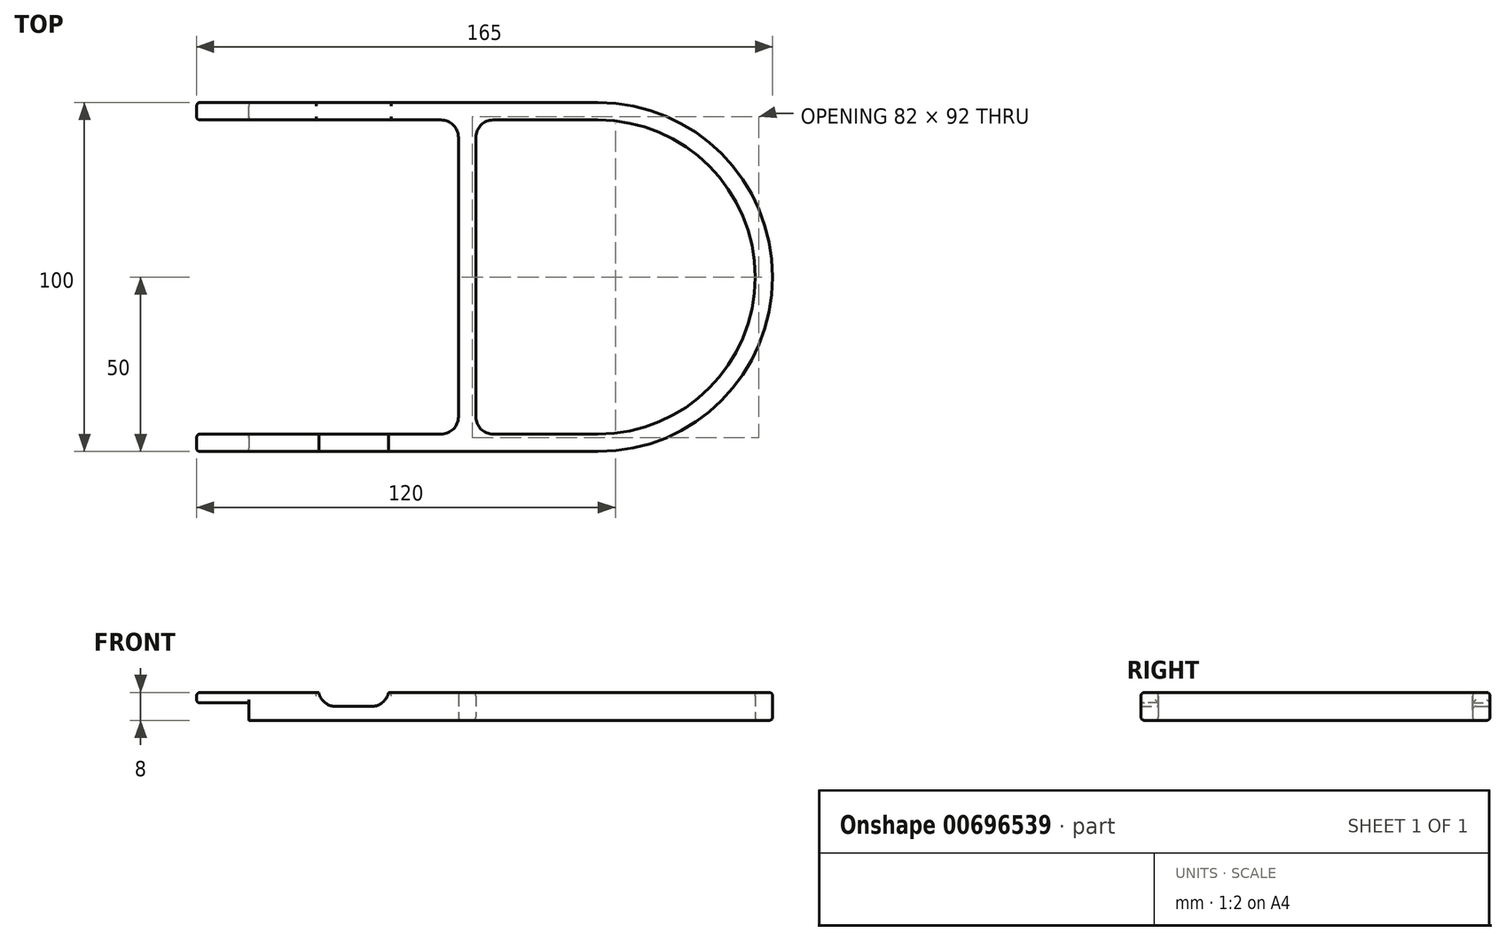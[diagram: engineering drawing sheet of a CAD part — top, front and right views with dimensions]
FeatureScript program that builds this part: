
annotation { "Feature Type Name" : "Feature", "Feature Type Description" : "" }
export const myFeature = defineFeature(function(context is Context, id is Id, definition is map)
    precondition{}
    {
        {
            var Q0;
            Q0=qCreatedBy(makeId("Top.planeOp"),FACE);
            var sketch = newSketch(context, id + "F0", { "sketchPlane" : qUnion([Q0])});
            skLineSegment(sketch, "E0", {"start": v(0, 0) * mm, "end": v(100, 0) * mm});
            skArc(sketch, "E1", {"start": v(100, 0) * mm, "mid": v(145, 45) * mm, "end": v(100, 90) * mm});
            skLineSegment(sketch, "E2", {"start": v(100, 90) * mm, "end": v(0, 90) * mm});
            skLineSegment(sketch, "E3", {"start": v(0, 90) * mm, "end": v(0, 95) * mm});
            skLineSegment(sketch, "E4", {"start": v(0, 95) * mm, "end": v(100, 95) * mm});
            skArc(sketch, "E5", {"start": v(100, -5) * mm, "mid": v(150, 45) * mm, "end": v(100, 95) * mm});
            skLineSegment(sketch, "E6", {"start": v(0, 0) * mm, "end": v(0, -5) * mm});
            skLineSegment(sketch, "E7", {"start": v(0, -5) * mm, "end": v(100, -5) * mm});
            skLineSegment(sketch, "E8.bottom", {"start": v(60, 0) * mm, "end": v(65, 0) * mm});
            skLineSegment(sketch, "E8.top", {"start": v(60, 90) * mm, "end": v(65, 90) * mm});
            skLineSegment(sketch, "E8.left", {"start": v(60, 0) * mm, "end": v(60, 90) * mm});
            skLineSegment(sketch, "E8.right", {"start": v(65, 0) * mm, "end": v(65, 90) * mm});
            skSolve(sketch);
        }
        {
            var Q0;
            Q0 = qSketchRegion(id + "F0", true);
            extrude(context, id + "F1", {"entities" : qUnion([Q0]), "depth" : 8 * mm, "offsetDistance" : 25 * mm});
        }
        {
            var Q0;
            Q0=makeQuery(id+"F1.opExtrude","SWEPT_FACE",FACE,{"disambiguationData":[OSD([sQuery(id+"F0.wireOp",EDGE,"E6")])]});
            var sketch = newSketch(context, id + "F2", { "sketchPlane" : qUnion([Q0])});
            skLineSegment(sketch, "E9.bottom", {"start": v(0, 8) * mm, "end": v(5, 8) * mm});
            skLineSegment(sketch, "E9.top", {"start": v(0, 5) * mm, "end": v(5, 5) * mm});
            skLineSegment(sketch, "E9.left", {"start": v(0, 8) * mm, "end": v(0, 5) * mm});
            skLineSegment(sketch, "E9.right", {"start": v(5, 8) * mm, "end": v(5, 5) * mm});
            skLineSegment(sketch, "E10.bottom", {"start": v(-90, 5) * mm, "end": v(-95, 5) * mm});
            skLineSegment(sketch, "E10.top", {"start": v(-90, 8) * mm, "end": v(-95, 8) * mm});
            skLineSegment(sketch, "E10.left", {"start": v(-90, 5) * mm, "end": v(-90, 8) * mm});
            skLineSegment(sketch, "E10.right", {"start": v(-95, 5) * mm, "end": v(-95, 8) * mm});
            skSolve(sketch);
        }
        {
            var Q0;
            Q0 = qSketchRegion(id + "F2", true);
            extrude(context, id + "F3", {"entities" : qUnion([Q0]), "operationType" : NewBodyOperationType.ADD, "depth" : 15 * mm, "offsetDistance" : 25 * mm});
        }
        {
            var Q0;
            Q0=makeQuery(id+"F1.opExtrude","SWEPT_EDGE",EDGE,{"disambiguationData":[OSD([sQuery(id+"F0.wireOp",EDGE,"E2"),sQuery(id+"F0.wireOp",EDGE,"E8.top"),sQuery(id+"F0.wireOp",EDGE,"E8.left")])]});
            var Q1;
            Q1=makeQuery(id+"F1.opExtrude","SWEPT_EDGE",EDGE,{"disambiguationData":[OSD([sQuery(id+"F0.wireOp",EDGE,"E2"),sQuery(id+"F0.wireOp",EDGE,"E8.top"),sQuery(id+"F0.wireOp",EDGE,"E8.right")])]});
            var Q2;
            Q2=makeQuery(id+"F1.opExtrude","SWEPT_EDGE",EDGE,{"disambiguationData":[OSD([sQuery(id+"F0.wireOp",EDGE,"E0"),sQuery(id+"F0.wireOp",EDGE,"E8.bottom"),sQuery(id+"F0.wireOp",EDGE,"E8.right")])]});
            var Q3;
            Q3=makeQuery(id+"F1.opExtrude","SWEPT_EDGE",EDGE,{"disambiguationData":[OSD([sQuery(id+"F0.wireOp",EDGE,"E0"),sQuery(id+"F0.wireOp",EDGE,"E8.bottom"),sQuery(id+"F0.wireOp",EDGE,"E8.left")])]});
            fillet(context, id + "F4", {"entities" : qUnion([Q0, Q1, Q2, Q3]), "radius" : 5 * mm, "tangentPropagation" : true, "allowEdgeOverflow" : false});
        }
        {
            var Q0;
            Q0=makeQuery(id+"F3.boolean.opBoolean","MERGE",FACE,{"derivedFrom":[makeQuery(id+"F1.opExtrude","SWEPT_FACE",FACE,{"disambiguationData":[OSD([sQuery(id+"F0.wireOp",EDGE,"E7")])]}),makeQuery(id+"F3.opExtrude","SWEPT_FACE",FACE,{"disambiguationData":[OSD([sQuery(id+"F2.wireOp",EDGE,"E9.right")])]})]});
            var sketch = newSketch(context, id + "F5", { "sketchPlane" : qUnion([Q0])});
            skLineSegment(sketch, "E11.bottom", {"start": v(20, 8) * mm, "end": v(40, 8) * mm});
            skLineSegment(sketch, "E11.top", {"start": v(20, 4) * mm, "end": v(40, 4) * mm});
            skLineSegment(sketch, "E11.left", {"start": v(20, 8) * mm, "end": v(20, 4) * mm});
            skLineSegment(sketch, "E11.right", {"start": v(40, 8) * mm, "end": v(40, 4) * mm});
            skSolve(sketch);
        }
        {
            var Q0;
            Q0 = qSketchRegion(id + "F5", true);
            extrude(context, id + "F6", {"entities" : qUnion([Q0]), "operationType" : NewBodyOperationType.REMOVE, "endBound" : BoundingType.THROUGH_ALL, "oppositeDirection" : true, "depth" : 25 * mm, "offsetDistance" : 25 * mm});
        }
        {
            var Q0;
            {var subQ1=sQuery(id+"F5.wireOp",EDGE,"E11.top");var subQ2=sQuery(id+"F5.wireOp",EDGE,"E11.left");Q0=makeQuery(id+"F6.boolean.opBoolean","COPY",EDGE,{"disambiguationData":[TD([makeQuery(id+"F1.opExtrude","SWEPT_FACE",FACE,{"disambiguationData":[OSD([sQuery(id+"F0.wireOp",EDGE,"E4")])]})])],"derivedFrom":makeQuery(id+"F6.opExtrude","SWEPT_EDGE",EDGE,{"disambiguationData":[OSD([subQ1,subQ2])]})});}
            var Q1;
            {var subQ1=sQuery(id+"F5.wireOp",EDGE,"E11.top");var subQ2=sQuery(id+"F5.wireOp",EDGE,"E11.right");Q1=makeQuery(id+"F6.boolean.opBoolean","COPY",EDGE,{"disambiguationData":[TD([makeQuery(id+"F1.opExtrude","SWEPT_FACE",FACE,{"disambiguationData":[OSD([sQuery(id+"F0.wireOp",EDGE,"E4")])]})])],"derivedFrom":makeQuery(id+"F6.opExtrude","SWEPT_EDGE",EDGE,{"disambiguationData":[OSD([subQ1,subQ2])]})});}
            var Q2;
            {var subQ1=sQuery(id+"F5.wireOp",EDGE,"E11.top");var subQ2=sQuery(id+"F5.wireOp",EDGE,"E11.right");Q2=makeQuery(id+"F6.boolean.opBoolean","COPY",EDGE,{"disambiguationData":[TD([makeQuery(id+"F1.opExtrude","SWEPT_FACE",FACE,{"disambiguationData":[OSD([sQuery(id+"F0.wireOp",EDGE,"E7")])]})])],"derivedFrom":makeQuery(id+"F6.opExtrude","SWEPT_EDGE",EDGE,{"disambiguationData":[OSD([subQ1,subQ2])]})});}
            var Q3;
            {var subQ1=sQuery(id+"F5.wireOp",EDGE,"E11.top");var subQ2=sQuery(id+"F5.wireOp",EDGE,"E11.left");Q3=makeQuery(id+"F6.boolean.opBoolean","COPY",EDGE,{"disambiguationData":[TD([makeQuery(id+"F1.opExtrude","SWEPT_FACE",FACE,{"disambiguationData":[OSD([sQuery(id+"F0.wireOp",EDGE,"E7")])]})])],"derivedFrom":makeQuery(id+"F6.opExtrude","SWEPT_EDGE",EDGE,{"disambiguationData":[OSD([subQ1,subQ2])]})});}
            var Q4;
            Q4=makeQuery(id+"F3.opExtrude","CAP_EDGE",EDGE,{"disambiguationData":[OSD([sQuery(id+"F2.wireOp",EDGE,"E9.top")])],"isStart":true});
            var Q5;
            Q5=makeQuery(id+"F3.opExtrude","CAP_EDGE",EDGE,{"disambiguationData":[OSD([sQuery(id+"F2.wireOp",EDGE,"E10.bottom")])],"isStart":true});
            fillet(context, id + "F7", {"entities" : qUnion([Q0, Q1, Q2, Q3, Q4, Q5]), "radius" : 5 * mm, "tangentPropagation" : true, "allowEdgeOverflow" : false});
        }
        {
            var Q0;
            {var subQ0=sQuery(id+"F0.wireOp",EDGE,"E2");Q0=makeQuery(id+"F1.opExtrude","CAP_EDGE",EDGE,{"disambiguationData":[OSD([subQ0]),TDD([makeQuery(id+"F0.imprint","IMPRINT",EDGE,{"disambiguationData":[TD([[makeQuery(id+"F0.imprint","INTERSECT",VERTEX,{"derivedFrom":[sQuery(id+"F0.wireOp",EDGE,"E1"),subQ0]}),-1.0]])],"derivedFrom":subQ0})])],"isStart":false});}
            var Q1;
            {var subQ0=sQuery(id+"F0.wireOp",EDGE,"E3");var subQ1=sQuery(id+"F0.wireOp",EDGE,"E2");var subQ4=makeQuery(id+"F0.imprint","IMPRINT",EDGE,{"disambiguationData":[TD([[makeQuery(id+"F0.imprint","INTERSECT",VERTEX,{"derivedFrom":[subQ1,subQ0]}),1.0]])],"derivedFrom":subQ1});var subQ5=sQuery(id+"F2.wireOp",EDGE,"E10.top");var subQ6=sQuery(id+"F2.wireOp",EDGE,"E10.left");Q1=makeQuery(id+"F6.boolean.opBoolean","SPLIT",EDGE,{"disambiguationData":[TD([makeQuery(id+"F6.opExtrude","SWEPT_FACE",FACE,{"disambiguationData":[OSD([sQuery(id+"F5.wireOp",EDGE,"E11.right")])]})])],"derivedFrom":makeQuery(id+"F3.boolean.opBoolean","MERGE",EDGE,{"derivedFrom":[makeQuery(id+"F1.opExtrude","CAP_EDGE",EDGE,{"disambiguationData":[OSD([subQ1]),TDD([subQ4])],"isStart":false}),makeQuery(id+"F3.opExtrude","SWEPT_EDGE",EDGE,{"disambiguationData":[OSD([subQ5,subQ6])]})]})});}
            var Q2;
            {var subQ0=sQuery(id+"F2.wireOp",EDGE,"E9.bottom");var subQ1=sQuery(id+"F0.wireOp",EDGE,"E7");var subQ2=sQuery(id+"F0.wireOp",EDGE,"E5");var subQ3=sQuery(id+"F2.wireOp",EDGE,"E9.right");Q2=makeQuery(id+"F6.boolean.opBoolean","SPLIT",EDGE,{"disambiguationData":[TD([makeQuery(id+"F1.opExtrude","SWEPT_FACE",FACE,{"disambiguationData":[OSD([subQ2])]})])],"derivedFrom":makeQuery(id+"F3.boolean.opBoolean","MERGE",EDGE,{"derivedFrom":[makeQuery(id+"F1.opExtrude","CAP_EDGE",EDGE,{"disambiguationData":[OSD([subQ1])],"isStart":false}),makeQuery(id+"F3.opExtrude","SWEPT_EDGE",EDGE,{"disambiguationData":[OSD([subQ0,subQ3])]})]})});}
            var Q3;
            Q3=makeQuery(id+"F1.opExtrude","CAP_EDGE",EDGE,{"disambiguationData":[OSD([sQuery(id+"F0.wireOp",EDGE,"E7")])],"isStart":true});
            var Q4;
            {var subQ0=sQuery(id+"F0.wireOp",EDGE,"E0");Q4=makeQuery(id+"F1.opExtrude","CAP_EDGE",EDGE,{"disambiguationData":[OSD([subQ0]),TDD([makeQuery(id+"F0.imprint","IMPRINT",EDGE,{"disambiguationData":[TD([[makeQuery(id+"F0.imprint","INTERSECT",VERTEX,{"derivedFrom":[subQ0,sQuery(id+"F0.wireOp",EDGE,"E1")]}),1.0]])],"derivedFrom":subQ0})])],"isStart":true});}
            var Q5;
            {var subQ0=sQuery(id+"F0.wireOp",EDGE,"E0");Q5=makeQuery(id+"F1.opExtrude","CAP_EDGE",EDGE,{"disambiguationData":[OSD([subQ0]),TDD([makeQuery(id+"F0.imprint","IMPRINT",EDGE,{"disambiguationData":[TD([[makeQuery(id+"F0.imprint","INTERSECT",VERTEX,{"derivedFrom":[subQ0,sQuery(id+"F0.wireOp",EDGE,"E6")]}),-1.0]])],"derivedFrom":subQ0})])],"isStart":true});}
            var Q6;
            {var subQ0=sQuery(id+"F2.wireOp",EDGE,"E9.bottom");var subQ2=sQuery(id+"F0.wireOp",EDGE,"E6");var subQ3=sQuery(id+"F0.wireOp",EDGE,"E0");var subQ4=sQuery(id+"F2.wireOp",EDGE,"E9.left");var subQ5=makeQuery(id+"F0.imprint","IMPRINT",EDGE,{"disambiguationData":[TD([[makeQuery(id+"F0.imprint","INTERSECT",VERTEX,{"derivedFrom":[subQ3,subQ2]}),-1.0]])],"derivedFrom":subQ3});Q6=makeQuery(id+"F6.boolean.opBoolean","SPLIT",EDGE,{"disambiguationData":[TD([makeQuery(id+"F6.opExtrude","SWEPT_FACE",FACE,{"disambiguationData":[OSD([sQuery(id+"F5.wireOp",EDGE,"E11.left")])]})])],"derivedFrom":makeQuery(id+"F3.boolean.opBoolean","MERGE",EDGE,{"derivedFrom":[makeQuery(id+"F1.opExtrude","CAP_EDGE",EDGE,{"disambiguationData":[OSD([subQ3]),TDD([subQ5])],"isStart":false}),makeQuery(id+"F3.opExtrude","SWEPT_EDGE",EDGE,{"disambiguationData":[OSD([subQ0,subQ4])]})]})});}
            var Q7;
            {var subQ0=sQuery(id+"F2.wireOp",EDGE,"E9.right");var subQ1=sQuery(id+"F2.wireOp",EDGE,"E9.bottom");var subQ2=sQuery(id+"F0.wireOp",EDGE,"E7");Q7=makeQuery(id+"F6.boolean.opBoolean","SPLIT",EDGE,{"disambiguationData":[TD([makeQuery(id+"F6.opExtrude","SWEPT_FACE",FACE,{"disambiguationData":[OSD([sQuery(id+"F5.wireOp",EDGE,"E11.left")])]})])],"derivedFrom":makeQuery(id+"F3.boolean.opBoolean","MERGE",EDGE,{"derivedFrom":[makeQuery(id+"F1.opExtrude","CAP_EDGE",EDGE,{"disambiguationData":[OSD([subQ2])],"isStart":false}),makeQuery(id+"F3.opExtrude","SWEPT_EDGE",EDGE,{"disambiguationData":[OSD([subQ1,subQ0])]})]})});}
            var Q8;
            {var subQ0=sQuery(id+"F2.wireOp",EDGE,"E10.right");var subQ1=sQuery(id+"F2.wireOp",EDGE,"E10.top");var subQ2=sQuery(id+"F0.wireOp",EDGE,"E4");Q8=makeQuery(id+"F6.boolean.opBoolean","SPLIT",EDGE,{"disambiguationData":[TD([makeQuery(id+"F6.opExtrude","SWEPT_FACE",FACE,{"disambiguationData":[OSD([sQuery(id+"F5.wireOp",EDGE,"E11.left")])]})])],"derivedFrom":makeQuery(id+"F3.boolean.opBoolean","MERGE",EDGE,{"derivedFrom":[makeQuery(id+"F1.opExtrude","CAP_EDGE",EDGE,{"disambiguationData":[OSD([subQ2])],"isStart":false}),makeQuery(id+"F3.opExtrude","SWEPT_EDGE",EDGE,{"disambiguationData":[OSD([subQ1,subQ0])]})]})});}
            var Q9;
            {var subQ0=sQuery(id+"F2.wireOp",EDGE,"E10.left");var subQ1=sQuery(id+"F2.wireOp",EDGE,"E10.top");var subQ2=sQuery(id+"F0.wireOp",EDGE,"E3");var subQ3=sQuery(id+"F0.wireOp",EDGE,"E2");var subQ5=makeQuery(id+"F0.imprint","IMPRINT",EDGE,{"disambiguationData":[TD([[makeQuery(id+"F0.imprint","INTERSECT",VERTEX,{"derivedFrom":[subQ3,subQ2]}),1.0]])],"derivedFrom":subQ3});Q9=makeQuery(id+"F6.boolean.opBoolean","SPLIT",EDGE,{"disambiguationData":[TD([makeQuery(id+"F6.opExtrude","SWEPT_FACE",FACE,{"disambiguationData":[OSD([sQuery(id+"F5.wireOp",EDGE,"E11.left")])]})])],"derivedFrom":makeQuery(id+"F3.boolean.opBoolean","MERGE",EDGE,{"derivedFrom":[makeQuery(id+"F1.opExtrude","CAP_EDGE",EDGE,{"disambiguationData":[OSD([subQ3]),TDD([subQ5])],"isStart":false}),makeQuery(id+"F3.opExtrude","SWEPT_EDGE",EDGE,{"disambiguationData":[OSD([subQ1,subQ0])]})]})});}
            fillet(context, id + "F8", {"entities" : qUnion([Q0, Q1, Q2, Q3, Q4, Q5, Q6, Q7, Q8, Q9]), "radius" : 1 * mm, "tangentPropagation" : true, "allowEdgeOverflow" : false});
        }
        {
            var Q0;
            {var subQ0=sQuery(id+"F0.wireOp",EDGE,"E2");Q0=makeQuery(id+"F6.boolean.opBoolean","INTERSECT",EDGE,{"derivedFrom":[makeQuery(id+"F3.boolean.opBoolean","MERGE",FACE,{"derivedFrom":[makeQuery(id+"F1.opExtrude","SWEPT_FACE",FACE,{"disambiguationData":[OSD([subQ0]),TDD([makeQuery(id+"F0.imprint","IMPRINT",EDGE,{"disambiguationData":[TD([[makeQuery(id+"F0.imprint","INTERSECT",VERTEX,{"derivedFrom":[subQ0,sQuery(id+"F0.wireOp",EDGE,"E3")]}),1.0]])],"derivedFrom":subQ0})])]}),makeQuery(id+"F3.opExtrude","SWEPT_FACE",FACE,{"disambiguationData":[OSD([sQuery(id+"F2.wireOp",EDGE,"E10.left")])]})]}),makeQuery(id+"F6.opExtrude","SWEPT_FACE",FACE,{"disambiguationData":[OSD([sQuery(id+"F5.wireOp",EDGE,"E11.top")])]})]});}
            var Q1;
            Q1=makeQuery(id+"F6.boolean.opBoolean","COPY",EDGE,{"derivedFrom":makeQuery(id+"F6.opExtrude","CAP_EDGE",EDGE,{"disambiguationData":[OSD([sQuery(id+"F5.wireOp",EDGE,"E11.top")])],"isStart":true})});
            var Q2;
            Q2=makeQuery(id+"F3.opExtrude","SWEPT_EDGE",EDGE,{"disambiguationData":[OSD([sQuery(id+"F0.wireOp",EDGE,"E6"),sQuery(id+"F0.wireOp",EDGE,"E7"),sQuery(id+"F2.wireOp",EDGE,"E9.top"),sQuery(id+"F2.wireOp",EDGE,"E9.right")])]});
            var Q3;
            {var subQ0=sQuery(id+"F0.wireOp",EDGE,"E2");Q3=makeQuery(id+"F7.opFillet","BLEND_EDGE",EDGE,{"blendedFrom":[makeQuery(id+"F3.opExtrude","CAP_EDGE",EDGE,{"disambiguationData":[OSD([sQuery(id+"F2.wireOp",EDGE,"E10.bottom")])],"isStart":true}),makeQuery(id+"F3.boolean.opBoolean","MERGE",FACE,{"derivedFrom":[makeQuery(id+"F1.opExtrude","SWEPT_FACE",FACE,{"disambiguationData":[OSD([subQ0]),TDD([makeQuery(id+"F0.imprint","IMPRINT",EDGE,{"disambiguationData":[TD([[makeQuery(id+"F0.imprint","INTERSECT",VERTEX,{"derivedFrom":[subQ0,sQuery(id+"F0.wireOp",EDGE,"E3")]}),1.0]])],"derivedFrom":subQ0})])]}),makeQuery(id+"F3.opExtrude","SWEPT_FACE",FACE,{"disambiguationData":[OSD([sQuery(id+"F2.wireOp",EDGE,"E10.left")])]})]})],"blendedInto":[makeQuery(id+"F3.boolean.opBoolean","MERGE",FACE,{"derivedFrom":[makeQuery(id+"F1.opExtrude","SWEPT_FACE",FACE,{"disambiguationData":[OSD([subQ0]),TDD([makeQuery(id+"F0.imprint","IMPRINT",EDGE,{"disambiguationData":[TD([[makeQuery(id+"F0.imprint","INTERSECT",VERTEX,{"derivedFrom":[subQ0,sQuery(id+"F0.wireOp",EDGE,"E3")]}),1.0]])],"derivedFrom":subQ0})])]}),makeQuery(id+"F3.opExtrude","SWEPT_FACE",FACE,{"disambiguationData":[OSD([sQuery(id+"F2.wireOp",EDGE,"E10.left")])]})]})]});}
            var Q4;
            Q4=makeQuery(id+"F3.opExtrude","CAP_FACE",FACE,{"disambiguationData":[OSD([sQuery(id+"F2.wireOp",EDGE,"E9.bottom"),sQuery(id+"F2.wireOp",EDGE,"E9.top"),sQuery(id+"F2.wireOp",EDGE,"E9.left"),sQuery(id+"F2.wireOp",EDGE,"E9.right")])],"isStart":false});
            var Q5;
            Q5=makeQuery(id+"F3.opExtrude","CAP_FACE",FACE,{"disambiguationData":[OSD([sQuery(id+"F2.wireOp",EDGE,"E10.bottom"),sQuery(id+"F2.wireOp",EDGE,"E10.top"),sQuery(id+"F2.wireOp",EDGE,"E10.left"),sQuery(id+"F2.wireOp",EDGE,"E10.right")])],"isStart":false});
            fillet(context, id + "F9", {"entities" : qUnion([Q0, Q1, Q2, Q3, Q4, Q5]), "radius" : 1 * mm, "tangentPropagation" : true, "allowEdgeOverflow" : false});
        }
    });
